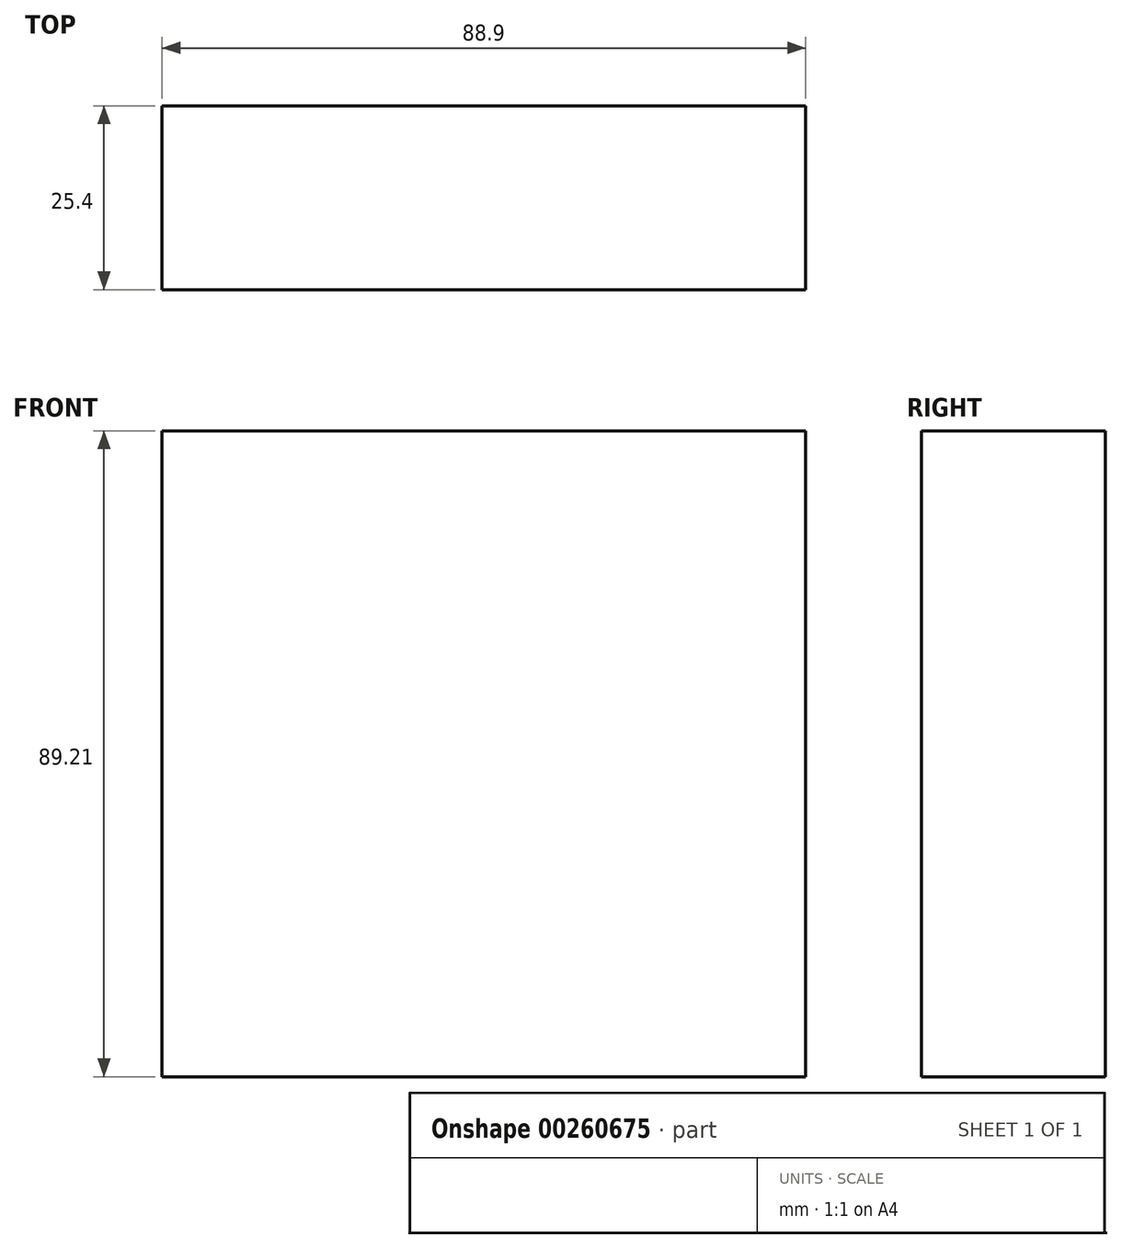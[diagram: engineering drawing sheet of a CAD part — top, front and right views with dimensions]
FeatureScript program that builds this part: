
annotation { "Feature Type Name" : "Feature", "Feature Type Description" : "" }
export const myFeature = defineFeature(function(context is Context, id is Id, definition is map)
    precondition{}
    {
        {
            var Q0;
            Q0=qCreatedBy(makeId("Front.planeOp"),FACE);
            var sketch = newSketch(context, id + "F0", { "sketchPlane" : qUnion([Q0])});
            skLineSegment(sketch, "E0.bottom", {"start": v(-45.59, 40.94) * mm, "end": v(43.31, 40.94) * mm});
            skLineSegment(sketch, "E0.top", {"start": v(-45.59, -48.27) * mm, "end": v(43.31, -48.27) * mm});
            skLineSegment(sketch, "E0.left", {"start": v(-45.59, 40.94) * mm, "end": v(-45.59, -48.27) * mm});
            skLineSegment(sketch, "E0.right", {"start": v(43.31, 40.94) * mm, "end": v(43.31, -48.27) * mm});
            skSolve(sketch);
        }
        {
            var Q0;
            Q0=makeQuery(id+"F0.imprint","IMPRINT",FACE,{"disambiguationData":[TD([[makeQuery(id+"F0.imprint","IMPRINT",EDGE,{"derivedFrom":sQuery(id+"F0.wireOp",EDGE,"E0.bottom")}),-1.0]])]});
            extrude(context, id + "F1", {"entities" : qUnion([Q0]), "depth" : 25.4 * mm});
        }
    });
